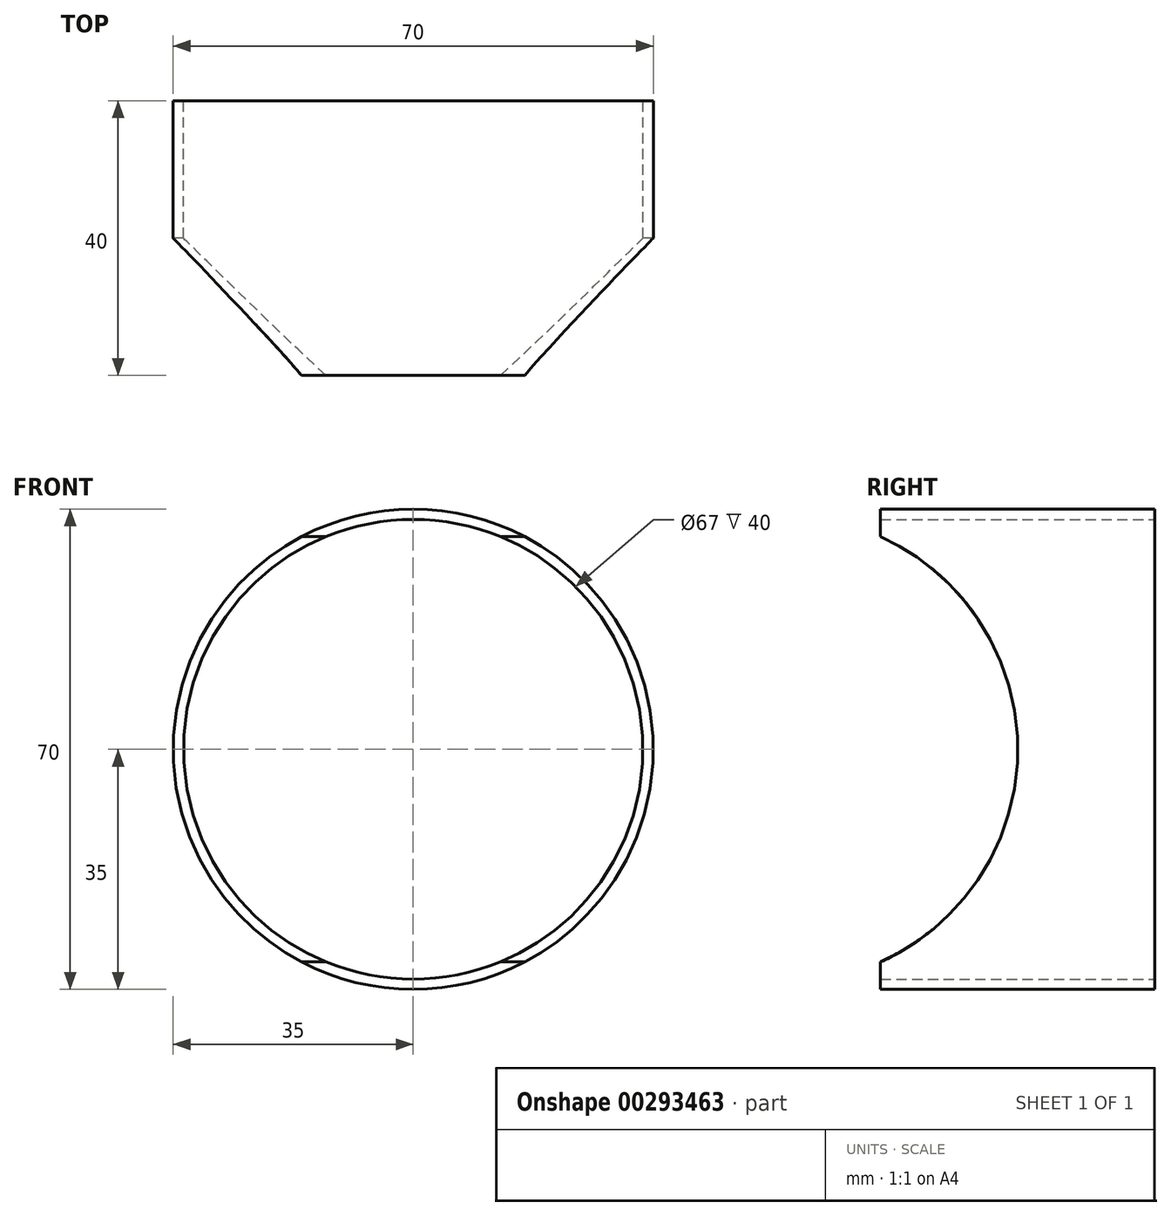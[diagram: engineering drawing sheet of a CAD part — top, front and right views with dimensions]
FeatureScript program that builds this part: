
annotation { "Feature Type Name" : "Feature", "Feature Type Description" : "" }
export const myFeature = defineFeature(function(context is Context, id is Id, definition is map)
    precondition{}
    {
        {
            var Q0;
            Q0=qCreatedBy(makeId("Front.planeOp"),FACE);
            var sketch = newSketch(context, id + "F0", { "sketchPlane" : qUnion([Q0])});
            skLineSegment(sketch, "E0", {"start": v(0, 0) * mm, "end": v(-129.05, 0) * mm, "construction": true});
            skLineSegment(sketch, "E1", {"start": v(0, 65.39) * mm, "end": v(0, -63.5) * mm, "construction": true});
            skCircle(sketch, "E2", {"center": v(0, 0) * mm, "radius": 35 * mm});
            skCircle(sketch, "E3", {"center": v(0, 0) * mm, "radius": 33.5 * mm});
            skSolve(sketch);
        }
        {
            var Q0;
            Q0=makeQuery(id+"F0.imprint","IMPRINT",FACE,{"disambiguationData":[TD([[makeQuery(id+"F0.imprint","IMPRINT",EDGE,{"derivedFrom":sQuery(id+"F0.wireOp",EDGE,"E2")}),1.0]])]});
            extrude(context, id + "F1", {"entities" : qUnion([Q0]), "endBound" : BoundingType.SYMMETRIC, "depth" : 40 * mm, "offsetDistance" : 25 * mm});
        }
        {
            var Q0;
            Q0=qCreatedBy(makeId("Right.planeOp"),FACE);
            var sketch = newSketch(context, id + "F2", { "sketchPlane" : qUnion([Q0])});
            skLineSegment(sketch, "E4", {"start": v(30.52, 0) * mm, "end": v(-53.74, 0) * mm, "construction": true});
            skCircle(sketch, "E5", {"center": v(-34, 0) * mm, "radius": 34 * mm});
            skSolve(sketch);
        }
        {
            var Q0;
            Q0=makeQuery(id+"F2.imprint","IMPRINT",FACE,{"disambiguationData":[TD([[makeQuery(id+"F2.imprint","IMPRINT",EDGE,{"derivedFrom":sQuery(id+"F2.wireOp",EDGE,"E5")}),1.0]])]});
            extrude(context, id + "F3", {"entities" : qUnion([Q0]), "operationType" : NewBodyOperationType.REMOVE, "endBound" : BoundingType.SYMMETRIC, "depth" : 80 * mm, "offsetDistance" : 25 * mm});
        }
    });
